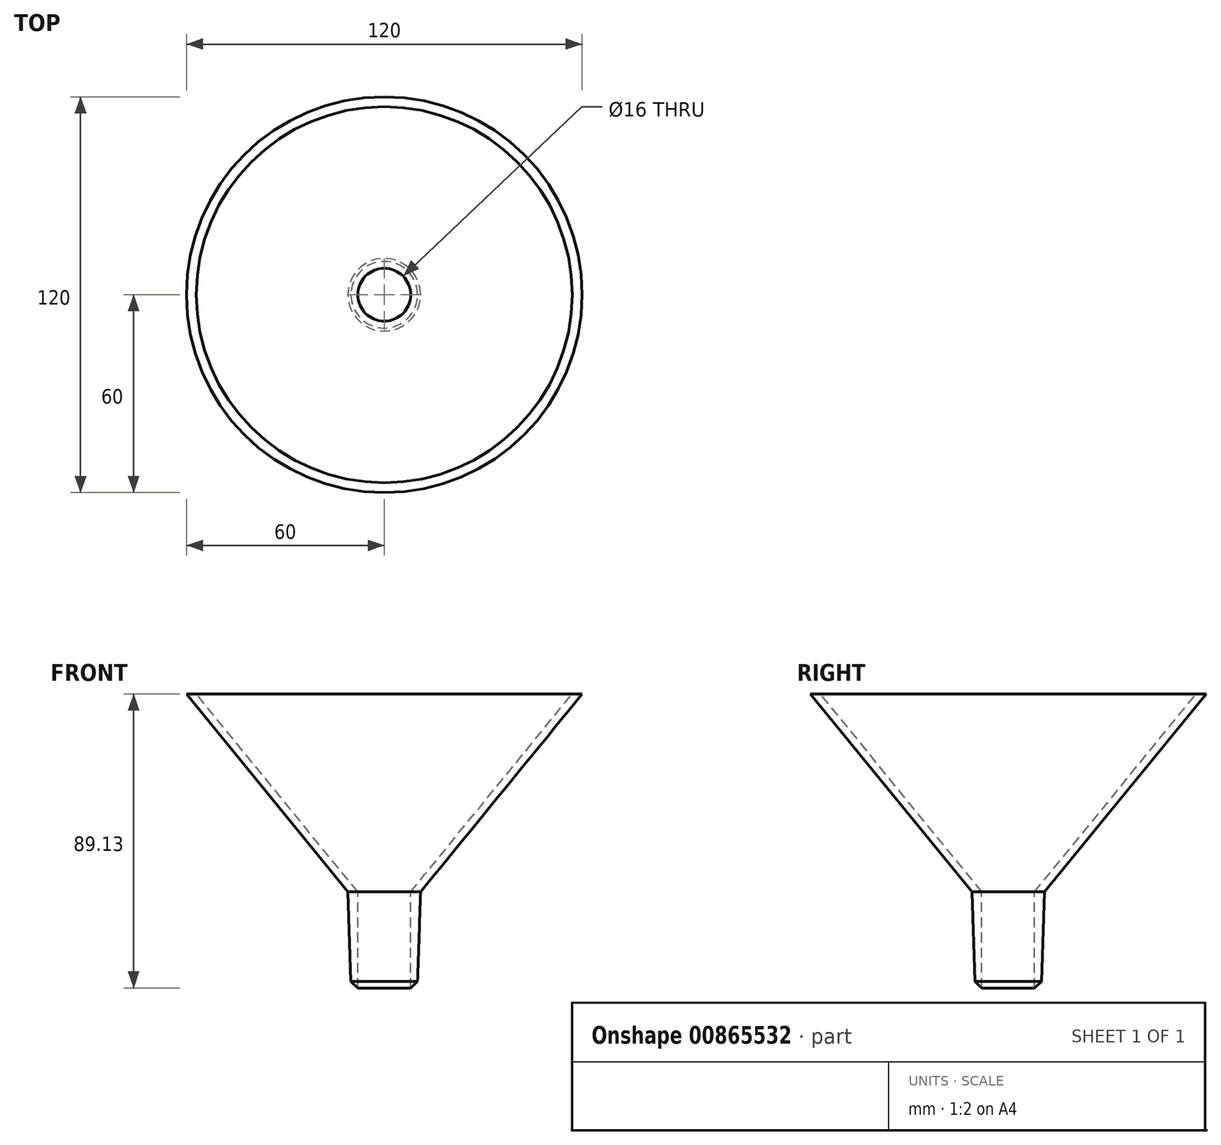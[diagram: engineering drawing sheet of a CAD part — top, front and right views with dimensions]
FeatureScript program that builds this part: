
annotation { "Feature Type Name" : "Feature", "Feature Type Description" : "" }
export const myFeature = defineFeature(function(context is Context, id is Id, definition is map)
    precondition{}
    {
        {
            var Q0;
            Q0=qCreatedBy(makeId("Front.planeOp"),FACE);
            var sketch = newSketch(context, id + "F0", { "sketchPlane" : qUnion([Q0])});
            skLineSegment(sketch, "E0", {"start": v(-8, -50.23) * mm, "end": v(-8, -20.23) * mm});
            skLineSegment(sketch, "E1", {"start": v(-8, -20.23) * mm, "end": v(-56.99, 39.77) * mm});
            skLineSegment(sketch, "E2", {"start": v(-56.99, 39.77) * mm, "end": v(-60, 39.77) * mm});
            skLineSegment(sketch, "E3", {"start": v(-60, 39.77) * mm, "end": v(-11, -20.24) * mm});
            skLineSegment(sketch, "E4", {"start": v(-11, -20.24) * mm, "end": v(-10, -50.23) * mm});
            skLineSegment(sketch, "E5", {"start": v(-10, -50.23) * mm, "end": v(-8, -50.23) * mm});
            skSolve(sketch);
        }
        {
            var Q0;
            Q0=makeQuery(id+"F0.imprint","IMPRINT",FACE,{"disambiguationData":[TD([[makeQuery(id+"F0.imprint","IMPRINT",EDGE,{"derivedFrom":sQuery(id+"F0.wireOp",EDGE,"E0")}),1.0]])]});
            var sketch = newSketch(context, id + "F1", { "sketchPlane" : qUnion([Q0])});
            skLineSegment(sketch, "E6", {"start": v(0, 0) * mm, "end": v(0, -71.88) * mm});
            skSolve(sketch);
        }
        {
            var Q0;
            Q0=makeQuery(id+"F0.imprint","IMPRINT",FACE,{"disambiguationData":[TD([[makeQuery(id+"F0.imprint","IMPRINT",EDGE,{"derivedFrom":sQuery(id+"F0.wireOp",EDGE,"E0")}),1.0]])]});
            var Q1;
            Q1=sQuery(id+"F1.wireOp",EDGE,"E6");
            revolve(context, id + "F2", {"surfaceOperationType" : NewSurfaceOperationType.NEW, "entities" : qUnion([Q0]), "axis" : qUnion([Q1]), "revolveType" : RevolveType.FULL});
        }
        {
            var Q0;
            Q0=makeQuery(id+"F2.opRevolve","SWEPT_EDGE",EDGE,{"disambiguationData":[OSD([sQuery(id+"F0.wireOp",EDGE,"E4"),sQuery(id+"F0.wireOp",EDGE,"E5")])]});
            chamfer(context, id + "F3", {"entities" : qUnion([Q0]), "width" : 3 * mm, "tangentPropagation" : true});
        }
    });
